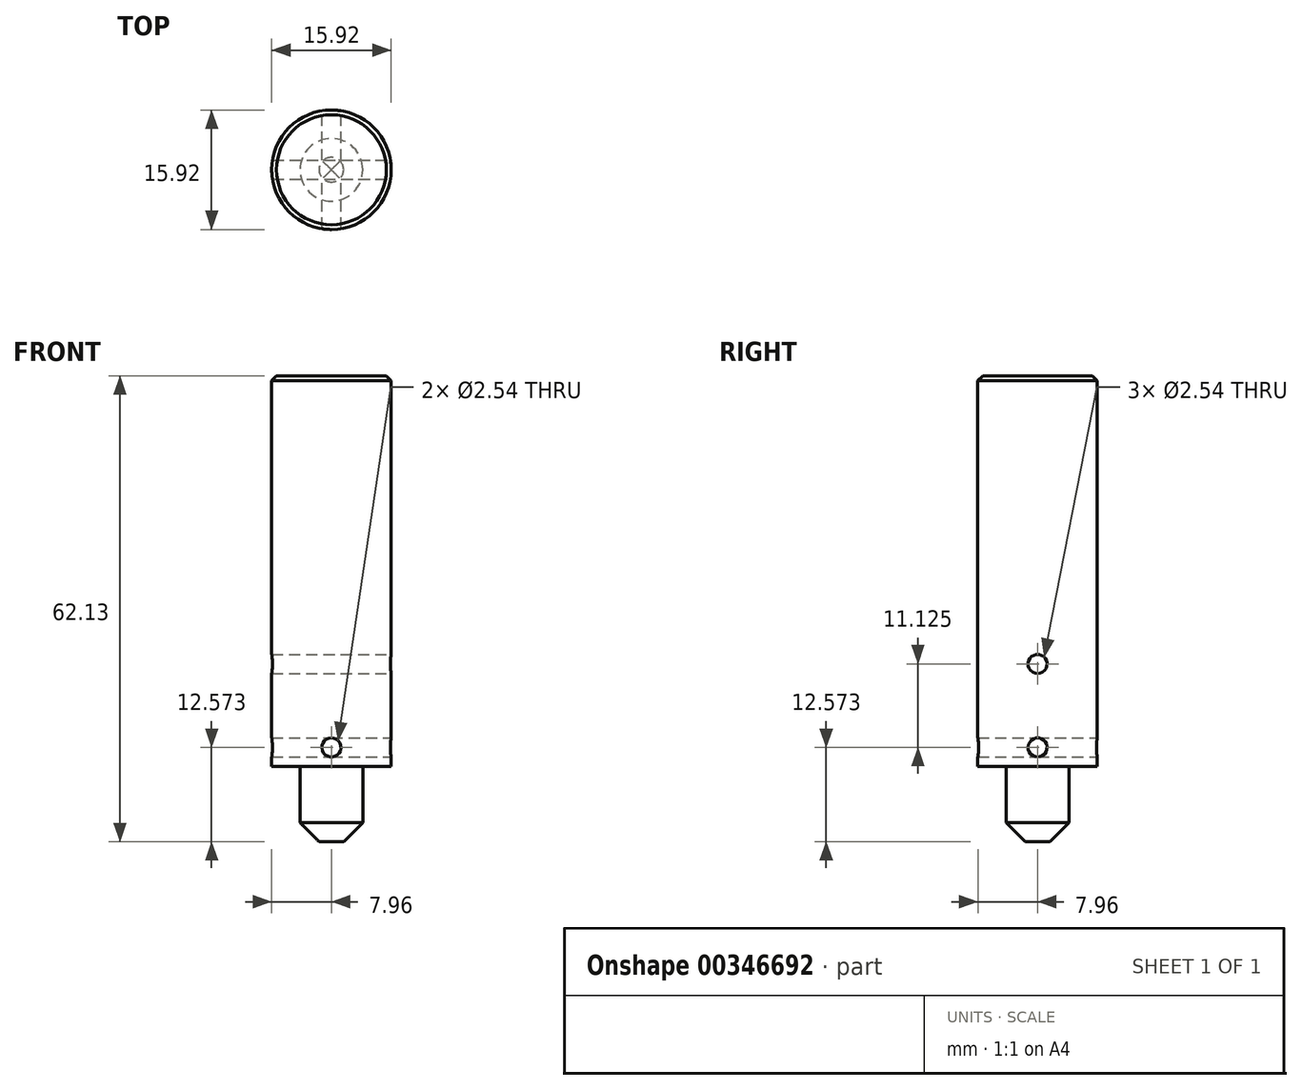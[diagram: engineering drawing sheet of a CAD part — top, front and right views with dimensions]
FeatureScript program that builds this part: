
annotation { "Feature Type Name" : "Feature", "Feature Type Description" : "" }
export const myFeature = defineFeature(function(context is Context, id is Id, definition is map)
    precondition{}
    {
        {
            var Q0;
            Q0=qCreatedBy(makeId("Front.planeOp"),FACE);
            var sketch = newSketch(context, id + "F0", { "sketchPlane" : qUnion([Q0])});
            skLineSegment(sketch, "E0.bottom", {"start": v(0, 0) * mm, "end": v(10.74, 0) * mm});
            skLineSegment(sketch, "E0.top", {"start": v(0, 62.13) * mm, "end": v(10.74, 62.13) * mm});
            skLineSegment(sketch, "E0.left", {"start": v(0, 0) * mm, "end": v(0, 62.13) * mm});
            skLineSegment(sketch, "E0.right", {"start": v(10.74, 0) * mm, "end": v(10.74, 62.13) * mm});
            skLineSegment(sketch, "E1", {"start": v(10.74, 62.13) * mm, "end": v(10.74, 48.49) * mm});
            skLineSegment(sketch, "E2", {"start": v(10.74, 48.49) * mm, "end": v(10.36, 48.49) * mm});
            skLineSegment(sketch, "E3", {"start": v(10.36, 48.49) * mm, "end": v(10.36, 46.58) * mm});
            skLineSegment(sketch, "E4", {"start": v(10.36, 46.58) * mm, "end": v(10.74, 46.58) * mm});
            skLineSegment(sketch, "E5", {"start": v(0, 0) * mm, "end": v(4.18, 0) * mm});
            skLineSegment(sketch, "E6", {"start": v(0, 62.13) * mm, "end": v(7.96, 62.13) * mm});
            skLineSegment(sketch, "E7", {"start": v(7.96, 62.13) * mm, "end": v(7.96, 10.06) * mm});
            skLineSegment(sketch, "E8", {"start": v(7.96, 10.06) * mm, "end": v(4.18, 10.06) * mm});
            skLineSegment(sketch, "E9", {"start": v(4.18, 0) * mm, "end": v(4.18, 10.06) * mm});
            skSolve(sketch);
        }
        {
            var Q0;
            {var subQ1=sQuery(id+"F0.wireOp",EDGE,"E0.bottom");Q0=makeQuery(id+"F0.imprint","IMPRINT",FACE,{"disambiguationData":[TD([[makeQuery(id+"F0.imprint","IMPRINT",EDGE,{"derivedFrom":subQ1}),1.0]])]});}
            var Q1;
            Q1=sQuery(id+"F0.wireOp",EDGE,"E0.left");
            revolve(context, id + "F1", {"entities" : qUnion([Q0]), "axis" : qUnion([Q1]), "revolveType" : RevolveType.FULL});
        }
        {
            var Q0;
            Q0=makeQuery(id+"F1.opRevolve","SWEPT_EDGE",EDGE,{"disambiguationData":[OSD([sQuery(id+"F0.wireOp",EDGE,"E0.bottom"),sQuery(id+"F0.wireOp",EDGE,"E0.right")])]});
            chamfer(context, id + "F2", {"entities" : qUnion([Q0]), "width" : 2.54 * mm, "tangentPropagation" : true});
        }
        {
            var Q0;
            Q0=makeQuery(id+"F1.opRevolve","SWEPT_FACE",FACE,{"disambiguationData":[OSD([sQuery(id+"F0.wireOp",EDGE,"E0.top")])]});
            chamfer(context, id + "F3", {"entities" : qUnion([Q0]), "width" : 0.64 * mm, "tangentPropagation" : true});
        }
        {
            var Q0;
            Q0=qCreatedBy(makeId("Right.planeOp"),FACE);
            var sketch = newSketch(context, id + "F4", { "sketchPlane" : qUnion([Q0])});
            skLineSegment(sketch, "E10", {"start": v(0, 0) * mm, "end": v(0, 11.3) * mm});
            skLineSegment(sketch, "E11", {"start": v(0, 11.3) * mm, "end": v(0, 12.57) * mm});
            skLineSegment(sketch, "E12", {"start": v(0, 12.57) * mm, "end": v(0, 13.84) * mm});
            skLineSegment(sketch, "E13", {"start": v(0, 13.84) * mm, "end": v(0, 22.43) * mm});
            skLineSegment(sketch, "E14", {"start": v(0, 22.43) * mm, "end": v(0, 23.7) * mm});
            skCircle(sketch, "E15", {"center": v(0, 12.57) * mm, "radius": 1.27 * mm});
            skCircle(sketch, "E16", {"center": v(0, 23.7) * mm, "radius": 1.27 * mm});
            skSolve(sketch);
        }
        {
            var Q0;
            Q0 = qSketchRegion(id + "F4", true);
            extrude(context, id + "F5", {"entities" : qUnion([Q0]), "operationType" : NewBodyOperationType.REMOVE, "endBound" : BoundingType.SYMMETRIC, "oppositeDirection" : true, "depth" : 25.4 * mm});
        }
        {
            var Q0;
            Q0=qCreatedBy(makeId("Front.planeOp"),FACE);
            var sketch = newSketch(context, id + "F6", { "sketchPlane" : qUnion([Q0])});
            skLineSegment(sketch, "E17", {"start": v(0, 0) * mm, "end": v(0, 11.3) * mm});
            skLineSegment(sketch, "E18", {"start": v(0, 11.3) * mm, "end": v(0, 12.57) * mm});
            skCircle(sketch, "E19", {"center": v(0, 12.57) * mm, "radius": 1.27 * mm});
            skSolve(sketch);
        }
        {
            var Q0;
            Q0 = qSketchRegion(id + "F6", true);
            extrude(context, id + "F7", {"entities" : qUnion([Q0]), "operationType" : NewBodyOperationType.REMOVE, "endBound" : BoundingType.SYMMETRIC, "depth" : 25.4 * mm});
        }
    });
